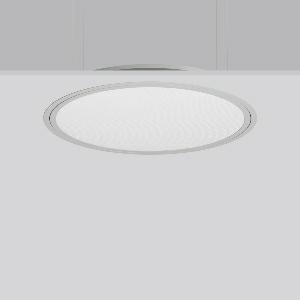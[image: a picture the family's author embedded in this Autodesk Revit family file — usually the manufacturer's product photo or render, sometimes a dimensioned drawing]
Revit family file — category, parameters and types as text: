
# Revit family: triona_round_e_312296_004_1_12_4930
name_source: partatom
category: Lighting Fixtures
units: mm (PartAtom-declared; Revit-internal decimal feet)

## family parameters
Cut with Voids When Loaded = No
Host = Face
Light Source = No
Part Type = Normal
Room Calculation Point = No
Round Connector Dimension = Use Diameter
Shared = No

## types (1)
- TRIONA round E (1 x LED Modul 840, 3900 lm, 4000)
    Apparent Load = 31 VA
    CIE Flux Codes = 58 86 97 100 100
    Color Rendering = 80
    Color Temperature = 4000
    Default Elevation = 1800 mm
    Description = Series: TRIONA round
Decorative round LED recessed surface luminaire. Cover made of sheet steel, powder-coated. Frame made of aluminium, powder-coated. Recessed ring: aluminium extrusion profile, powder coated. Light emission through a diffuser in plastic, opal/prismatic. Lightguide and diffuser made of non-yellowing plastic (PMMA). Lateral light emission (RZB SIDELITE technology) for above-average homogeneous light distribution. Suitable for installation in cavity ceilings. Tool-free mounting system thanks to the rocker arm mechanism (patent pending). Electronic ballast included. Very easy installation thanks to Plug+Play connection. Perfect for office areas (RUG < 19) and environments with computer screens in accordance with EN 12464-1. 
Colour: silver, matt (approx. RAL 9006)
Diameter: 725 mm
Height: 2 mm
Cut-out diameter: 702 mm
Recess height: 100 mm
Luminaire: recess height: 89 mm
Lamp: LED
Socket: without socket
Colour temperature: 4000K
Colour rendering index (CRI): 80
System power: 31 W
Rated luminous flux: 3900 lm
Luminous efficiency: 126 lm/W
Control gear: Converter, dimmable, DALI
Protection class: I
Type of protection: IP 40
    Height = 0 mm  [stored 0 ft]
    Lamp = 1 x LED Modul 840
    Lamp Light Flux = 3900 lm
    Lamp count = 1
    Length = 725 mm
    Lifetime = 50000 h
    Luminous efficacy = 126 lm/W
    Manufacturer = RZB
    ModVariant = No
    Model = 312296.004.1.12
    Mounting Place = Ceiling
    Mounting Type = Recessed
    Number of Poles = 1
    OnlyDefault = Yes
    Power Factor = 1
    Product Name = TRIONA round E
    Product group = Recessed modular luminaires
    ProductGroupID = 406
    Protection Class = Protection class I
    Protection Degree = IP 20
    RLX_Detail_Level = 1
    RLX_Emergency_Light_Flux = 0 lm
    RLX_Emergency_Type = 0
    RLX_Emergency_Type_DB = No
    RlxData = <blob elided: 37157 chars, md5=85e7f5f8>
    Socket = socket
    Standby Power = 0 W
    System Light Flux = 3900 lm
    System Power = 31 W
    Type Comments = Product without accessories
    Type Image = 312296.004.12.jpg
    URL = http://relux.com
    VarID = ---
    Voltage = 230 V
    Voltage Range = 220-240 V
    Weight = 0.00 kg
    Width = 0 mm  [stored 0 ft]

note: [stored X ft] marks values corroborated as IEEE doubles in the binary element streams (Revit-internal decimal feet)

## geometry (parser evidence)
native form markers: Blend x4, Sweep x10
no freeform markers — native parametric forms only
